# Revit family: IS_Finesse_E3442_BIM_NL
name_source: partatom
category: Plumbing Fixtures
units: mm (PartAtom-declared; Revit-internal decimal feet)

## family parameters
Cut with Voids When Loaded = No
Host = Face
Maintain Annotation Orientation = No
OmniClass Number = 23.45.05.14.21.11
OmniClass Title = Bath/Shower Units
Part Type = Normal
Room Calculation Point = No
Round Connector Dimension = Use Diameter
Shared = Yes

## types (6) — shared parameters
Accessories = https://www.idealstandard.nl
Afmetingen = 1600 x 300 x 600mm
AfstandsEenheid = millimeter
AreaUnits = millimeters
Artikelomschrijving = FINESSE | Kast 600x300x1600 mm, 1 deur
Assembly Code = C1030200
AssetType = Fixed
Auteur = Ideal Standard
BIMObjectName = ISI_IdealStandard_Furniture_Finesse_E3442
BREEAM = No
Beschrijvinggarantie = Fabrieksgarantie
BimObjectNaam = ISI_IdealStandard_Furniture_Finesse_E3442
Brand = Ideal Standard
Breedte = 600
ConnectionType = Plumbing
CurrencyUnit = €
Default Elevation = 1219 mm
Description = FINESSE | Cabinet 600x300x1600 mm, 1 door
Diepte = 299,999999999968
DurationUnit = year
DuurEenheid = jaar
ECA = No
EPD = https://www.idealstandard.nl
ExpectedLife = 30
Garantieunits = Jaar
GemaaktOp = 2024/09/04
Help = https://www.idealstandard.nl
Hoogte = 1600
Hulp = https://www.idealstandard.nl
IfcExportAs = IfcFurnitureType
Installatieinstructies = https://www.idealstandard.nl
InstallationInstructions = https://www.idealstandard.nl
Lengte = 299,999999999968
LinearUnits = millimeters
Manufacturer = Ideal Standard
ManufacturerURL = https://www.idealstandard.nl
Materiaal = hout
Merk = Ideal Standard
ModelReference = FINESSE | Cabinet 600x300x1600 mm, 1 door
NBSDescription = Baths
Name = ISI_Furniture_Finesse_E3442_IdealStandard
NominalDepth = 300 mm
NominalHeight = 1600 mm  [stored 5.24934 ft]
NominalLength = 300 mm
NominalWidth = 600 mm
ProductInformation = https://www.idealstandard.nl
ProductSoort = Meubilair
Productinformatie = https://www.idealstandard.nl
Shape = Rectangular
Size = 1600 x 300 x 600mm
Space = Internal
SpareParts = https://www.idealstandard.nl
TMV3 = No
Telefoonnummer = 077 355 08 08
Typeconnectie = Sanitair
URL = https://www.idealstandard.nl
Uniclass2015Code = Pr_40_20_76
Uniclass2015Title = Sanitary accessories
Uniclass2015Version = Products v1.34
Urlproducent = https://www.idealstandard.nl
ValutaEenheid = €
Versie = 1
Version = 1
VolumeUnits = Litres
Volumeunits = Liter
Vorm = Rechthoekig
WRAS = No
WarrantyDescription = Manufacturers Warranty
WarrantyDurationParts = 25
WarrantyDurationUnit = year
WarrantyGuarantorParts = https://www.idealstandard.nl
WaterEfficientProduct = No
Wisselstukken = https://www.idealstandard.nl
zero-valued in all types: Vervangingskosten

## per-type parameters (varying)
| type | Afwerking | Artikelnummer | Artikelreferentie | BarCode | Color | Eigenschappen | Features | Finish | Kleur | MAT | Model | ModelNumber | NettWeight | Nettogewicht |
| E3442UP - FINESSE COLUMN 1 DOOR GEMT | Greige mat | E3442UP | FINESSE / Kast 600x300x1600 mm in mat greige afwerking, 1 deur / Softclose, Voorgemonteerd, Duurzaam geproduceerd hout | 5017830568056 | greige matt | FINESSE / Kast 600x300x1600 mm in mat greige afwerking, 1 deur / Softclose, Voorgemonteerd, Duurzaam geproduceerd hout | FINESSE / Cabinet 600x300x1600 mm in greige matt finish, 1 door / Soft close, Assembled, Sustainably sourced wood | greige matt | Greige mat | UP | E3442UP | E3442UP | 36.20 Kg | 36.20 Kg |
| E3442UQ - FINESSE COLUMN 1 DOOR ABMT | Mat asblauw | E3442UQ | FINESSE / Kast 600x300x1600 mm in matt ashblue afwerking, 1 deur / Softclose, Voorgemonteerd, Duurzaam geproduceerd hout | 5017830568063 | matt ashblue | FINESSE / Kast 600x300x1600 mm in matt ashblue afwerking, 1 deur / Softclose, Voorgemonteerd, Duurzaam geproduceerd hout | FINESSE / Cabinet 600x300x1600 mm in matt ashblue finish, 1 door / Soft close, Assembled, Sustainably sourced wood | matt ashblue | Mat asblauw | UQ | E3442UQ | E3442UQ | 34.83 Kg | 34.83 Kg |
| E3442UR - FINESSE COLUMN 1 DOOR DKEM | Donkere iep | E3442UR | FINESSE / Kast 600x300x1600 mm in dark elm afwerking, 1 deur / Softclose, Voorgemonteerd, Duurzaam geproduceerd hout | 5017830568070 | dark elm | FINESSE / Kast 600x300x1600 mm in dark elm afwerking, 1 deur / Softclose, Voorgemonteerd, Duurzaam geproduceerd hout | FINESSE / Cabinet 600x300x1600 mm in dark elm finish, 1 door / Soft close, Assembled, Sustainably sourced wood | dark elm | Donkere iep | UR | E3442UR | E3442UR | 48.64 Kg | 48.64 Kg |
| E3442US - FINESSE COLUMN 1 DOOR WOAK | Witte eik | E3442US | FINESSE / Kast 600x300x1600 mm in white oak afwerking, 1 deur / Softclose, Voorgemonteerd, Duurzaam geproduceerd hout | 5017830568087 | white oak | FINESSE / Kast 600x300x1600 mm in white oak afwerking, 1 deur / Softclose, Voorgemonteerd, Duurzaam geproduceerd hout | FINESSE / Cabinet 600x300x1600 mm in white oak finish, 1 door / Soft close, Assembled, Sustainably sourced wood | white oak | Witte eik | US | E3442US | E3442US | 44.24 Kg | 44.24 Kg |
| E3442Y1 - FINESSE COLUMN 1 DOOR WHMT | Mat wit | E3442Y1 | FINESSE / Kast 600x300x1600 mm in matt white afwerking, 1 deur / Softclose, Voorgemonteerd, Duurzaam geproduceerd hout | 5017830568094 | matt white | FINESSE / Kast 600x300x1600 mm in matt white afwerking, 1 deur / Softclose, Voorgemonteerd, Duurzaam geproduceerd hout | FINESSE / Cabinet 600x300x1600 mm in matt white finish, 1 door / Soft close, Assembled, Sustainably sourced wood | matt white | Mat wit | Y1 | E3442Y1 | E3442Y1 | 36.20 Kg | 36.20 Kg |
| E3442Y2 - FINESSE COLUMN 1 DOOR ANMT | Mat antraciet | E3442Y2 | FINESSE / Kast 600x300x1600 mm in matt anthracite afwerking, 1 deur / Softclose, Voorgemonteerd, Duurzaam geproduceerd hout | 5017830568100 | matt anthracite | FINESSE / Kast 600x300x1600 mm in matt anthracite afwerking, 1 deur / Softclose, Voorgemonteerd, Duurzaam geproduceerd hout | FINESSE / Cabinet 600x300x1600 mm in matt anthracite finish, 1 door / Soft close, Assembled, Sustainably sourced wood | matt anthracite | Mat antraciet | Y2 | E3442Y2 | E3442Y2 | 36.20 Kg | 36.20 Kg |

note: [stored X ft] marks values corroborated as IEEE doubles in the binary element streams (Revit-internal decimal feet)

## geometry (parser evidence)
native form markers: Sweep x3
no freeform markers — native parametric forms only
